# Revit family: Presostat RT
name_source: partatom
category: Pipe Accessories
units: mm (PartAtom-declared; Revit-internal decimal feet)

## family parameters
Always vertical = Yes
Cut with Voids When Loaded = No
Part Type = Normal
Round Connector Dimension = Use Diameter
Shared = No
Work Plane-Based = No

## types (2) — shared parameters
Ambient temperature range = -50 °C - 70 °C
IfcExportAs = IfcValveType
IfcExportType = RT
Manufacturer = Danfoss
Max working pressure = 22.0 bar
Pressure connection type = G 3/8"
Regulation range = 0.20 bar - 6.00 bar
URL = https://www.danfoss.com

## per-type parameters (varying)
| type | Description | Differential pressure | Enclosure rating | Model | Reset function |
| RT200 0,2-6,0 bar G 3/8" Auto_017-523766 | RT200 0,2-6,0 bar G 3/8" Auto | 0.25 bar - 1.20 bar | IP66 | 017-523766 | Auto |
| RT200 0,2-6,0 bar G 3/8" Reset_017-523966 | RT200 0,2-6,0 bar G 3/8" Reset | - 0.25 bar | IP54 | 017-523966 | Min Reset |

## geometry (parser evidence)
native form markers: Sweep x2
no freeform markers — native parametric forms only
